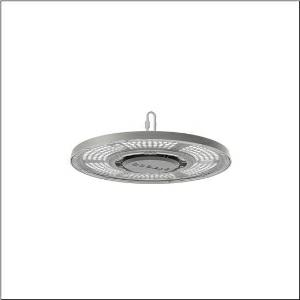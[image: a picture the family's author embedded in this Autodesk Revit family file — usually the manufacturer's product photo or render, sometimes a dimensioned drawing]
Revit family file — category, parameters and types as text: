
# Revit family: highbay_31-s_51hc42da4fmb
name_source: partatom
category: Lighting Fixtures
units: mm (PartAtom-declared; Revit-internal decimal feet)

## family parameters
Cut with Voids When Loaded = No
Host = Face
Light Source = No
Part Type = Normal
Room Calculation Point = No
Round Connector Dimension = Use Diameter
Shared = No

## types (1)
- Highbay 31-S (1 x LED, 14000 lm, 94 W, 4000K)
    Apparent Load = 94 VA
    CIE Flux Codes = 77 99 100 100 100
    Color Rendering = 80
    Color Temperature = 4000K
    Default Elevation = 1800 mm
    Description = Highbay 31-S, high bay luminaire, primary light control with lens, of PC, primary optical cover: cover panel, of PC, transparent, light emission: direct distribution, primary light characteristic: rotationally symmetric, installation type: suspended mounting, surface-mounted, LED, rated luminous flux: 14.000lm, luminous efficacy: 150lm/W, light colour: 840, colour temperature: 4000K, control gear: DALI 2, with cable, 5x 1.0mm², free wire ends, mains connection: 220..240V, AC, 50/60Hz, cable length: 1,5m, rated input power: 94W, housing, rotationally symmetric, of diecast aluminium, powder-coated, grey aluminium (RAL 9007), with hook on luminaire side, incl. screw, diameter: 339mm, protection rating (complete): IP65, insulation class (complete): insulation class I (protective earthing), certification: CE, ENEC, UKCA, protection symbol: D, impact resistance: IK08, permissible operating ambient temperature: -30..+45°C, corresponds to IFS (International Featured Standards) requirements for safety and quality in the food industry, packaging unit: 1 piece
    Height = 141 mm
    Lamp = 1 x LED
    Lamp Light Flux = 14000 lm
    Lamp Power = 94 W
    Lamp count = 1
    Length = 339 mm
    Luminous efficacy = 149 lm/W
    Manufacturer = Siteco
    ModVariant = No
    Model = 51HC42DA4FMB
    Mounting Place = Ceiling
    Mounting Type = Pendant
    Number of Poles = 1
    OnlyDefault = Yes
    Power Factor = 1
    Product Name = Highbay 31-S
    Product group = high bay luminaire
    ProductGroupID = 902
    Protection Class = Protection class I
    Protection Degree = IP 65
    RLX_Detail_Level = 1
    RLX_Emergency_Light_Flux = 0 lm
    RLX_Emergency_Type = 0
    RLX_Emergency_Type_DB = No
    RlxData = <blob elided: 163033 chars, md5=35ef4583>
    Socket = socket
    Standby Power = 0 W
    System Light Flux = 14000 lm
    System Power = 94 W
    Type Comments = Product without accessories
    Type Image = l_1007237.jpg
    URL = http://relux.com
    VarID = ---
    Voltage = 0 V
    Weight = 0.00 kg
    Width = 0 mm  [stored 0 ft]

note: [stored X ft] marks values corroborated as IEEE doubles in the binary element streams (Revit-internal decimal feet)

## geometry (parser evidence)
native form markers: Blend x4, Sweep x9
no freeform markers — native parametric forms only
